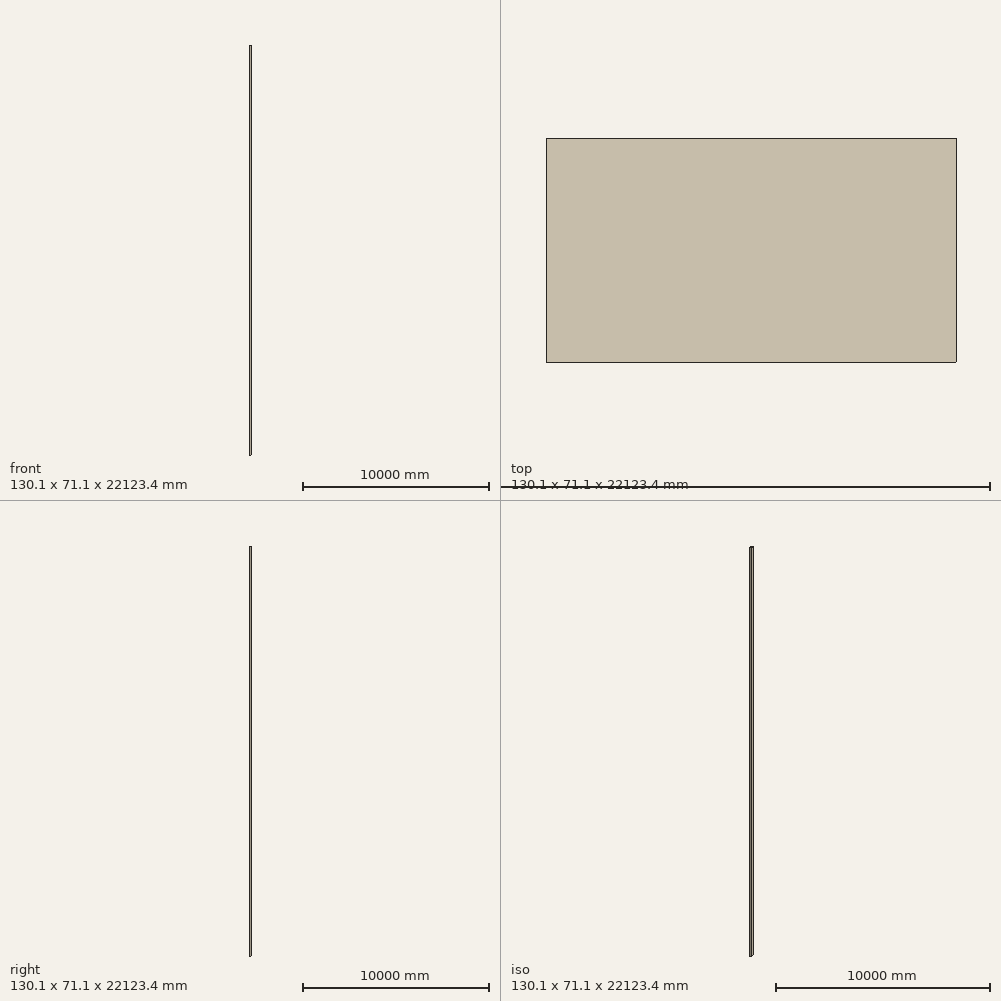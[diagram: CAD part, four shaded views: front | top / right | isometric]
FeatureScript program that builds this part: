
annotation { "Feature Type Name" : "Feature", "Feature Type Description" : "" }
export const myFeature = defineFeature(function(context is Context, id is Id, definition is map)
    precondition{}
    {
        {
            var Q0;
            Q0=qCreatedBy(makeId("Top.planeOp"),FACE);
            var sketch = newSketch(context, id + "F0", { "sketchPlane" : qUnion([Q0])});
            skLineSegment(sketch, "E0.bottom", {"start": v(-61.53, 34.5) * mm, "end": v(68.58, 34.5) * mm});
            skLineSegment(sketch, "E0.top", {"start": v(-61.53, -36.56) * mm, "end": v(68.58, -36.56) * mm});
            skLineSegment(sketch, "E0.left", {"start": v(-61.53, 34.5) * mm, "end": v(-61.53, -36.56) * mm});
            skLineSegment(sketch, "E0.right", {"start": v(68.58, 34.5) * mm, "end": v(68.58, -36.56) * mm});
            skSolve(sketch);
        }
        {
            var Q0;
            Q0=makeQuery(id+"F0.imprint","IMPRINT",FACE,{"disambiguationData":[TD([[makeQuery(id+"F0.imprint","IMPRINT",EDGE,{"derivedFrom":sQuery(id+"F0.wireOp",EDGE,"E0.bottom")}),-1.0]])]});
            extrude(context, id + "F1", {"entities" : qUnion([Q0]), "depth" : 22123.4 * mm, "offsetDistance" : 25.4 * mm});
        }
    });
